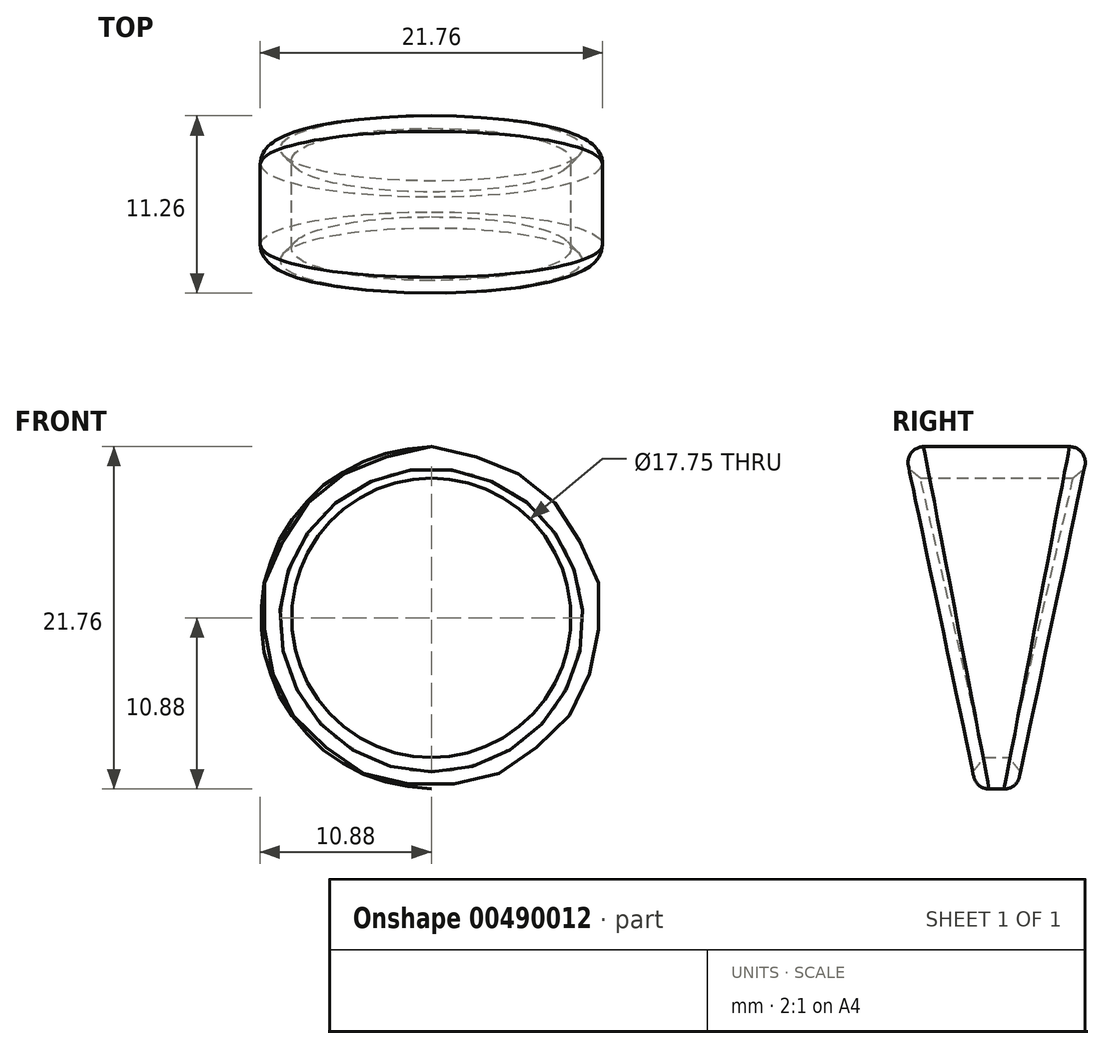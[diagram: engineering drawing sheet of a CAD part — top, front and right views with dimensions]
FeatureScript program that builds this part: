
annotation { "Feature Type Name" : "Feature", "Feature Type Description" : "" }
export const myFeature = defineFeature(function(context is Context, id is Id, definition is map)
    precondition{}
    {
        {
            var Q0;
            Q0=qCreatedBy(makeId("Front.planeOp"),FACE);
            var sketch = newSketch(context, id + "F0", { "sketchPlane" : qUnion([Q0])});
            skCircle(sketch, "E0", {"center": v(0, 0) * mm, "radius": 8.88 * mm});
            skCircle(sketch, "E1.0", {"center": v(0, 0) * mm, "radius": 10.88 * mm});
            skSolve(sketch);
        }
        {
            var Q0;
            Q0=makeQuery(id+"F0.imprint","IMPRINT",FACE,{"disambiguationData":[TD([[makeQuery(id+"F0.imprint","IMPRINT",EDGE,{"derivedFrom":sQuery(id+"F0.wireOp",EDGE,"E0")}),-1.0]])]});
            extrude(context, id + "F1", {"entities" : qUnion([Q0]), "depth" : 6 * mm, "hasSecondDirection" : true, "secondDirectionOppositeDirection" : true, "secondDirectionDepth" : 6 * mm});
        }
        {
            var Q0;
            Q0=qCreatedBy(makeId("Right.planeOp"),FACE);
            var sketch = newSketch(context, id + "F2", { "sketchPlane" : qUnion([Q0])});
            skLineSegment(sketch, "E2", {"start": v(0, -17) * mm, "end": v(6.51, 13.95) * mm});
            skLineSegment(sketch, "E3", {"start": v(6.51, 13.95) * mm, "end": v(0, 13.95) * mm});
            skLineSegment(sketch, "E4.MirrorCS", {"start": v(-6.51, 13.95) * mm, "end": v(0, 13.95) * mm});
            skLineSegment(sketch, "E5.MirrorCS", {"start": v(0, -17) * mm, "end": v(-6.51, 13.95) * mm});
            skLineSegment(sketch, "E6.bottom", {"start": v(-10.4, 16.56) * mm, "end": v(9.47, 16.56) * mm});
            skLineSegment(sketch, "E6.top", {"start": v(-10.4, -19.19) * mm, "end": v(9.47, -19.19) * mm});
            skLineSegment(sketch, "E6.left", {"start": v(-10.4, 16.56) * mm, "end": v(-10.4, -19.19) * mm});
            skLineSegment(sketch, "E6.right", {"start": v(9.47, 16.56) * mm, "end": v(9.47, -19.19) * mm});
            skSolve(sketch);
        }
        {
            var Q0;
            Q0=makeQuery(id+"F2.imprint","IMPRINT",FACE,{"disambiguationData":[TD([[makeQuery(id+"F2.imprint","IMPRINT",EDGE,{"derivedFrom":sQuery(id+"F2.wireOp",EDGE,"E2")}),-1.0]])]});
            extrude(context, id + "F3", {"entities" : qUnion([Q0]), "operationType" : NewBodyOperationType.REMOVE, "oppositeDirection" : true, "depth" : 25 * mm, "hasSecondDirection" : true, "secondDirectionOppositeDirection" : false, "secondDirectionDepth" : 25 * mm});
        }
        {
            var Q0;
            Q0=makeQuery(id+"F3.boolean.opBoolean","INTERSECT",EDGE,{"derivedFrom":[makeQuery(id+"F1.opExtrude","SWEPT_FACE",FACE,{"disambiguationData":[OSD([sQuery(id+"F0.wireOp",EDGE,"E1.0")])]}),makeQuery(id+"F3.opExtrude","SWEPT_FACE",FACE,{"disambiguationData":[OSD([sQuery(id+"F2.wireOp",EDGE,"E2")])]})]});
            var Q1;
            Q1=makeQuery(id+"F3.boolean.opBoolean","INTERSECT",EDGE,{"derivedFrom":[makeQuery(id+"F1.opExtrude","SWEPT_FACE",FACE,{"disambiguationData":[OSD([sQuery(id+"F0.wireOp",EDGE,"E1.0")])]}),makeQuery(id+"F3.opExtrude","SWEPT_FACE",FACE,{"disambiguationData":[OSD([sQuery(id+"F2.wireOp",EDGE,"E5.MirrorCS")])]})]});
            fillet(context, id + "F4", {"entities" : qUnion([Q0, Q1]), "radius" : 1 * mm, "tangentPropagation" : true, "allowEdgeOverflow" : false});
        }
        {
            var Q0;
            Q0=makeQuery(id+"F3.boolean.opBoolean","INTERSECT",EDGE,{"derivedFrom":[makeQuery(id+"F1.opExtrude","SWEPT_FACE",FACE,{"disambiguationData":[OSD([sQuery(id+"F0.wireOp",EDGE,"E0")])]}),makeQuery(id+"F3.opExtrude","SWEPT_FACE",FACE,{"disambiguationData":[OSD([sQuery(id+"F2.wireOp",EDGE,"E2")])]})]});
            var Q1;
            Q1=makeQuery(id+"F3.boolean.opBoolean","INTERSECT",EDGE,{"derivedFrom":[makeQuery(id+"F1.opExtrude","SWEPT_FACE",FACE,{"disambiguationData":[OSD([sQuery(id+"F0.wireOp",EDGE,"E0")])]}),makeQuery(id+"F3.opExtrude","SWEPT_FACE",FACE,{"disambiguationData":[OSD([sQuery(id+"F2.wireOp",EDGE,"E5.MirrorCS")])]})]});
            chamfer(context, id + "F5", {"entities" : qUnion([Q0, Q1]), "width" : .75 * mm, "tangentPropagation" : true});
        }
    });
